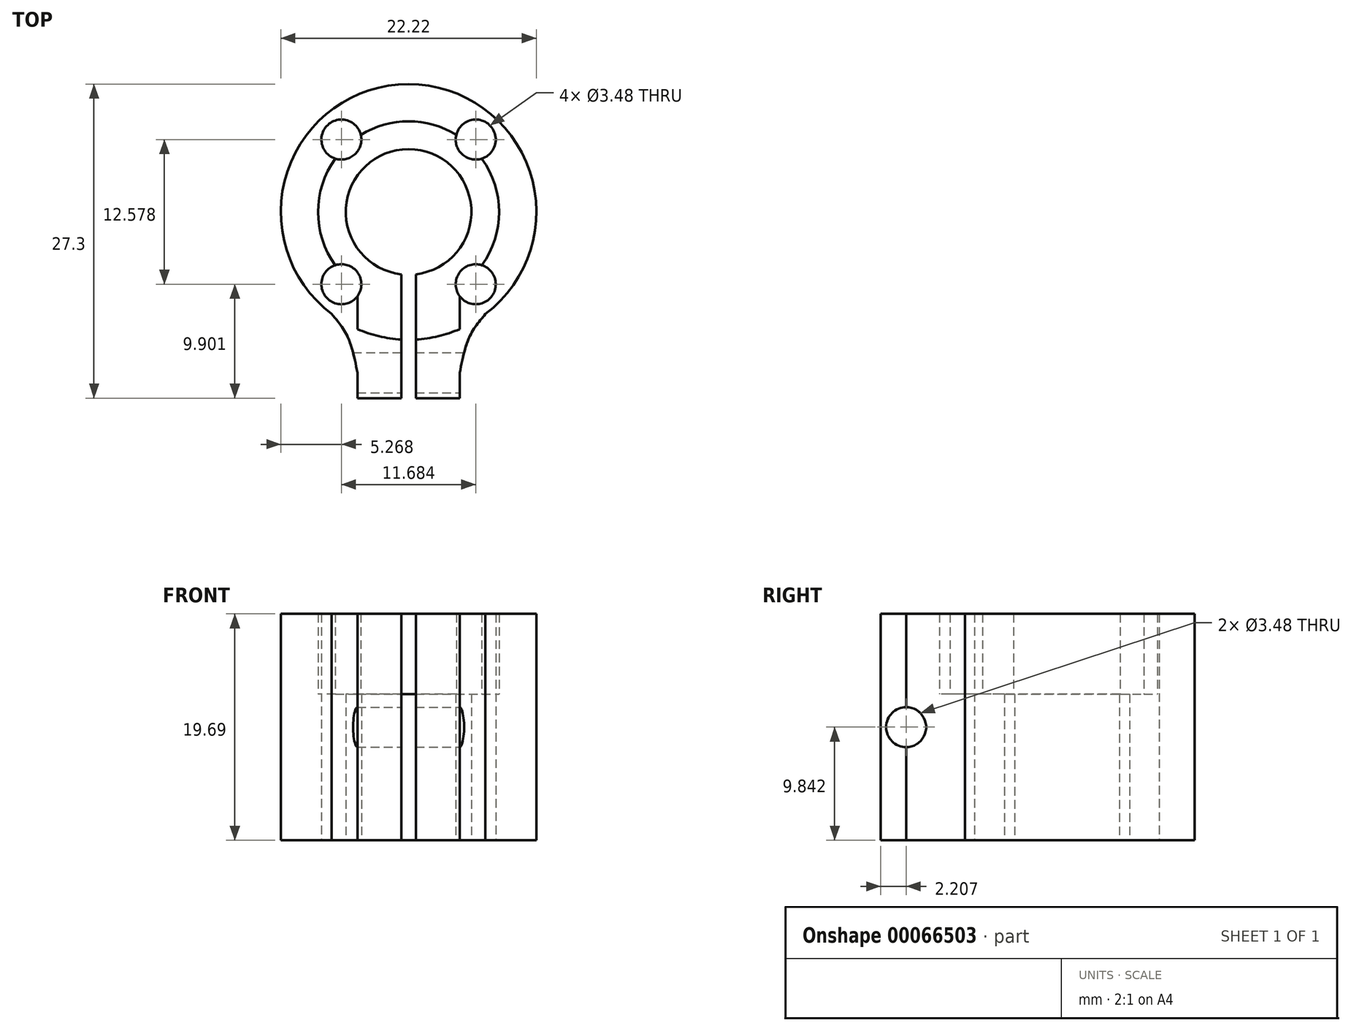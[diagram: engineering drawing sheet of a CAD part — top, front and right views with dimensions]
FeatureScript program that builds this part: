
annotation { "Feature Type Name" : "Feature", "Feature Type Description" : "" }
export const myFeature = defineFeature(function(context is Context, id is Id, definition is map)
    precondition{}
    {
        {
            var Q0;
            Q0=qCreatedBy(makeId("Top.planeOp"),FACE);
            var sketch = newSketch(context, id + "F0", { "sketchPlane" : qUnion([Q0])});
            skCircle(sketch, "E0", {"center": v(0, 0) * mm, "radius": 11.11 * mm});
            skLineSegment(sketch, "E1.rect.bottom", {"start": v(4.45, -16.2) * mm, "end": v(-4.44, -16.2) * mm});
            skLineSegment(sketch, "E1.rect.top", {"start": v(4.44, 16.2) * mm, "end": v(-4.45, 16.2) * mm});
            skLineSegment(sketch, "E1.rect.left", {"start": v(4.44, -16.2) * mm, "end": v(4.44, 16.2) * mm});
            skLineSegment(sketch, "E1.rect.right", {"start": v(-4.45, -16.2) * mm, "end": v(-4.44, 16.2) * mm});
            skLineSegment(sketch, "E2.rect.bottom", {"start": v(-0.63, 16.2) * mm, "end": v(0.63, 16.2) * mm});
            skLineSegment(sketch, "E2.rect.top", {"start": v(-0.63, -16.2) * mm, "end": v(0.63, -16.2) * mm});
            skLineSegment(sketch, "E2.rect.left", {"start": v(-0.63, 16.2) * mm, "end": v(-0.63, -16.2) * mm});
            skLineSegment(sketch, "E2.rect.right", {"start": v(0.63, 16.2) * mm, "end": v(0.63, -16.2) * mm});
            skLineSegment(sketch, "E3", {"start": v(0, 24.4) * mm, "end": v(0, -38.1) * mm, "construction": true});
            skFitSpline(sketch, "E4", {"points": [v(-6.69, -8.88) * mm, v(-5.33, -10.8) * mm, v(-4.45, -13.98) * mm], "startDerivative": vector(3.26, -3.85) * mm, "endDerivative": vector(1.27, -6.31) * mm});
            skFitSpline(sketch, "E5.MirrorCS", {"points": [v(6.69, -8.88) * mm, v(5.33, -10.8) * mm, v(4.45, -13.98) * mm], "startDerivative": vector(-3.26, -3.85) * mm, "endDerivative": vector(-1.27, -6.31) * mm});
            skCircle(sketch, "E6", {"center": v(-5.84, 6.29) * mm, "radius": 1.74 * mm});
            skCircle(sketch, "E7.MirrorC", {"center": v(5.84, 6.29) * mm, "radius": 1.74 * mm});
            skCircle(sketch, "E8.MirrorC", {"center": v(-5.84, -6.29) * mm, "radius": 1.74 * mm});
            skCircle(sketch, "E9.MirrorC", {"center": v(5.84, -6.29) * mm, "radius": 1.74 * mm});
            skCircle(sketch, "E10", {"center": v(0, 0) * mm, "radius": 7.87 * mm});
            skCircle(sketch, "E11", {"center": v(0, 0) * mm, "radius": 5.46 * mm});
            skSolve(sketch);
        }
        {
            var Q0;
            {var subQ0=sQuery(id+"F0.wireOp",EDGE,"E0");var subQ1=makeQuery(id+"F0.imprint","INTERSECT",VERTEX,{"derivedFrom":[subQ0,sQuery(id+"F0.wireOp",EDGE,"E4")]});Q0=makeQuery(id+"F0.imprint","IMPRINT",FACE,{"disambiguationData":[TD([[makeQuery(id+"F0.imprint","IMPRINT",EDGE,{"disambiguationData":[TD([[subQ1,1.0]])],"derivedFrom":subQ0}),1.0]])]});}
            var Q1;
            {var subQ1=sQuery(id+"F0.wireOp",EDGE,"E0");var subQ5=sQuery(id+"F0.wireOp",EDGE,"E1.rect.right");var subQ6=makeQuery(id+"F0.imprint","INTERSECT",VERTEX,{"disambiguationData":[OD(0.0)],"derivedFrom":[subQ1,subQ5]});Q1=makeQuery(id+"F0.imprint","IMPRINT",FACE,{"disambiguationData":[TD([[makeQuery(id+"F0.imprint","IMPRINT",EDGE,{"disambiguationData":[TD([[subQ6,1.0]])],"derivedFrom":subQ1}),1.0]])]});}
            var Q2;
            {var subQ1=sQuery(id+"F0.wireOp",EDGE,"E0");var subQ6=sQuery(id+"F0.wireOp",EDGE,"E1.rect.left");var subQ8=makeQuery(id+"F0.imprint","INTERSECT",VERTEX,{"disambiguationData":[OD(0.0)],"derivedFrom":[subQ1,subQ6]});Q2=makeQuery(id+"F0.imprint","IMPRINT",FACE,{"disambiguationData":[TD([[makeQuery(id+"F0.imprint","IMPRINT",EDGE,{"disambiguationData":[TD([[subQ8,-1.0]])],"derivedFrom":subQ1}),1.0]])]});}
            var Q3;
            {var subQ0=sQuery(id+"F0.wireOp",EDGE,"E0");var subQ1=makeQuery(id+"F0.imprint","INTERSECT",VERTEX,{"derivedFrom":[subQ0,sQuery(id+"F0.wireOp",EDGE,"E5.MirrorCS")]});Q3=makeQuery(id+"F0.imprint","IMPRINT",FACE,{"disambiguationData":[TD([[makeQuery(id+"F0.imprint","IMPRINT",EDGE,{"disambiguationData":[TD([[subQ1,1.0]])],"derivedFrom":subQ0}),1.0]])]});}
            var Q4;
            {var subQ0=sQuery(id+"F0.wireOp",EDGE,"E2.rect.right");var subQ1=sQuery(id+"F0.wireOp",EDGE,"E0");var subQ2=makeQuery(id+"F0.imprint","INTERSECT",VERTEX,{"disambiguationData":[OD(0.0)],"derivedFrom":[subQ1,subQ0]});Q4=makeQuery(id+"F0.imprint","IMPRINT",FACE,{"disambiguationData":[TD([[makeQuery(id+"F0.imprint","IMPRINT",EDGE,{"disambiguationData":[TD([[subQ2,-1.0]])],"derivedFrom":subQ1}),1.0]])]});}
            var Q5;
            {var subQ0=sQuery(id+"F0.wireOp",EDGE,"E4");Q5=makeQuery(id+"F0.imprint","IMPRINT",FACE,{"disambiguationData":[TD([[makeQuery(id+"F0.imprint","IMPRINT",EDGE,{"derivedFrom":subQ0}),1.0]])]});}
            var Q6;
            {var subQ0=sQuery(id+"F0.wireOp",EDGE,"E1.rect.right");var subQ6=sQuery(id+"F0.wireOp",EDGE,"E0");var subQ7=makeQuery(id+"F0.imprint","INTERSECT",VERTEX,{"disambiguationData":[OD(1.0)],"derivedFrom":[subQ6,subQ0]});Q6=makeQuery(id+"F0.imprint","IMPRINT",FACE,{"disambiguationData":[TD([[makeQuery(id+"F0.imprint","IMPRINT",EDGE,{"disambiguationData":[TD([[subQ7,-1.0]])],"derivedFrom":subQ6}),-1.0]])]});}
            var Q7;
            {var subQ2=sQuery(id+"F0.wireOp",EDGE,"E0");var subQ6=sQuery(id+"F0.wireOp",EDGE,"E2.rect.right");var subQ7=makeQuery(id+"F0.imprint","INTERSECT",VERTEX,{"disambiguationData":[OD(1.0)],"derivedFrom":[subQ2,subQ6]});Q7=makeQuery(id+"F0.imprint","IMPRINT",FACE,{"disambiguationData":[TD([[makeQuery(id+"F0.imprint","IMPRINT",EDGE,{"disambiguationData":[TD([[subQ7,-1.0]])],"derivedFrom":subQ2}),-1.0]])]});}
            var Q8;
            {var subQ0=sQuery(id+"F0.wireOp",EDGE,"E5.MirrorCS");Q8=makeQuery(id+"F0.imprint","IMPRINT",FACE,{"disambiguationData":[TD([[makeQuery(id+"F0.imprint","IMPRINT",EDGE,{"derivedFrom":subQ0}),-1.0]])]});}
            extrude(context, id + "F1", {"entities" : qUnion([Q0, Q1, Q2, Q3, Q4, Q5, Q6, Q7, Q8]), "depth" : 7 * mm});
        }
        {
            var Q0;
            {var subQ0=sQuery(id+"F0.wireOp",EDGE,"E8.MirrorC");var subQ1=sQuery(id+"F0.wireOp",EDGE,"E1.rect.right");var subQ2=makeQuery(id+"F0.imprint","INTERSECT",VERTEX,{"disambiguationData":[OD(1.0)],"derivedFrom":[subQ1,subQ0]});Q0=makeQuery(id+"F0.imprint","IMPRINT",FACE,{"disambiguationData":[TD([[makeQuery(id+"F0.imprint","IMPRINT",EDGE,{"disambiguationData":[TD([[subQ2,-1.0]])],"derivedFrom":subQ1}),1.0]])]});}
            var Q1;
            {var subQ5=sQuery(id+"F0.wireOp",EDGE,"E1.rect.right");var subQ7=sQuery(id+"F0.wireOp",EDGE,"E11");var subQ8=makeQuery(id+"F0.imprint","INTERSECT",VERTEX,{"disambiguationData":[OD(1.0)],"derivedFrom":[subQ5,subQ7]});Q1=makeQuery(id+"F0.imprint","IMPRINT",FACE,{"disambiguationData":[TD([[makeQuery(id+"F0.imprint","IMPRINT",EDGE,{"disambiguationData":[TD([[subQ8,-1.0]])],"derivedFrom":subQ5}),-1.0]])]});}
            var Q2;
            {var subQ5=sQuery(id+"F0.wireOp",EDGE,"E1.rect.left");var subQ7=sQuery(id+"F0.wireOp",EDGE,"E11");var subQ9=makeQuery(id+"F0.imprint","INTERSECT",VERTEX,{"disambiguationData":[OD(1.0)],"derivedFrom":[subQ5,subQ7]});Q2=makeQuery(id+"F0.imprint","IMPRINT",FACE,{"disambiguationData":[TD([[makeQuery(id+"F0.imprint","IMPRINT",EDGE,{"disambiguationData":[TD([[subQ9,-1.0]])],"derivedFrom":subQ5}),1.0]])]});}
            var Q3;
            {var subQ0=sQuery(id+"F0.wireOp",EDGE,"E9.MirrorC");var subQ1=sQuery(id+"F0.wireOp",EDGE,"E1.rect.left");var subQ2=makeQuery(id+"F0.imprint","INTERSECT",VERTEX,{"disambiguationData":[OD(1.0)],"derivedFrom":[subQ1,subQ0]});Q3=makeQuery(id+"F0.imprint","IMPRINT",FACE,{"disambiguationData":[TD([[makeQuery(id+"F0.imprint","IMPRINT",EDGE,{"disambiguationData":[TD([[subQ2,-1.0]])],"derivedFrom":subQ1}),-1.0]])]});}
            var Q4;
            {var subQ3=sQuery(id+"F0.wireOp",EDGE,"E9.MirrorC");var subQ5=sQuery(id+"F0.wireOp",EDGE,"E1.rect.left");var subQ6=makeQuery(id+"F0.imprint","INTERSECT",VERTEX,{"disambiguationData":[OD(1.0)],"derivedFrom":[subQ5,subQ3]});Q4=makeQuery(id+"F0.imprint","IMPRINT",FACE,{"disambiguationData":[TD([[makeQuery(id+"F0.imprint","IMPRINT",EDGE,{"disambiguationData":[TD([[subQ6,-1.0]])],"derivedFrom":subQ5}),1.0]])]});}
            var Q5;
            {var subQ3=sQuery(id+"F0.wireOp",EDGE,"E8.MirrorC");var subQ5=sQuery(id+"F0.wireOp",EDGE,"E1.rect.right");var subQ6=makeQuery(id+"F0.imprint","INTERSECT",VERTEX,{"disambiguationData":[OD(1.0)],"derivedFrom":[subQ5,subQ3]});Q5=makeQuery(id+"F0.imprint","IMPRINT",FACE,{"disambiguationData":[TD([[makeQuery(id+"F0.imprint","IMPRINT",EDGE,{"disambiguationData":[TD([[subQ6,-1.0]])],"derivedFrom":subQ5}),-1.0]])]});}
            var Q6;
            {var subQ1=sQuery(id+"F0.wireOp",EDGE,"E0");var subQ5=sQuery(id+"F0.wireOp",EDGE,"E1.rect.right");var subQ6=makeQuery(id+"F0.imprint","INTERSECT",VERTEX,{"disambiguationData":[OD(1.0)],"derivedFrom":[subQ1,subQ5]});Q6=makeQuery(id+"F0.imprint","IMPRINT",FACE,{"disambiguationData":[TD([[makeQuery(id+"F0.imprint","IMPRINT",EDGE,{"disambiguationData":[TD([[subQ6,-1.0]])],"derivedFrom":subQ1}),1.0]])]});}
            var Q7;
            {var subQ5=sQuery(id+"F0.wireOp",EDGE,"E0");var subQ7=sQuery(id+"F0.wireOp",EDGE,"E2.rect.right");var subQ8=makeQuery(id+"F0.imprint","INTERSECT",VERTEX,{"disambiguationData":[OD(1.0)],"derivedFrom":[subQ5,subQ7]});Q7=makeQuery(id+"F0.imprint","IMPRINT",FACE,{"disambiguationData":[TD([[makeQuery(id+"F0.imprint","IMPRINT",EDGE,{"disambiguationData":[TD([[subQ8,-1.0]])],"derivedFrom":subQ5}),1.0]])]});}
            var Q8;
            {var subQ1=sQuery(id+"F0.wireOp",EDGE,"E0");var subQ11=makeQuery(id+"F0.imprint","INTERSECT",VERTEX,{"derivedFrom":[subQ1,sQuery(id+"F0.wireOp",EDGE,"E5.MirrorCS")]});Q8=makeQuery(id+"F0.imprint","IMPRINT",FACE,{"disambiguationData":[TD([[makeQuery(id+"F0.imprint","IMPRINT",EDGE,{"disambiguationData":[TD([[subQ11,1.0]])],"derivedFrom":subQ1}),1.0]])]});}
            var Q9;
            {var subQ1=sQuery(id+"F0.wireOp",EDGE,"E1.rect.left");var subQ5=sQuery(id+"F0.wireOp",EDGE,"E0");var subQ6=makeQuery(id+"F0.imprint","INTERSECT",VERTEX,{"disambiguationData":[OD(0.0)],"derivedFrom":[subQ5,subQ1]});Q9=makeQuery(id+"F0.imprint","IMPRINT",FACE,{"disambiguationData":[TD([[makeQuery(id+"F0.imprint","IMPRINT",EDGE,{"disambiguationData":[TD([[subQ6,-1.0]])],"derivedFrom":subQ5}),1.0]])]});}
            var Q10;
            {var subQ1=sQuery(id+"F0.wireOp",EDGE,"E1.rect.right");var subQ6=sQuery(id+"F0.wireOp",EDGE,"E0");var subQ9=makeQuery(id+"F0.imprint","INTERSECT",VERTEX,{"disambiguationData":[OD(0.0)],"derivedFrom":[subQ6,subQ1]});Q10=makeQuery(id+"F0.imprint","IMPRINT",FACE,{"disambiguationData":[TD([[makeQuery(id+"F0.imprint","IMPRINT",EDGE,{"disambiguationData":[TD([[subQ9,1.0]])],"derivedFrom":subQ6}),1.0]])]});}
            var Q11;
            {var subQ1=sQuery(id+"F0.wireOp",EDGE,"E0");var subQ8=makeQuery(id+"F0.imprint","INTERSECT",VERTEX,{"derivedFrom":[subQ1,sQuery(id+"F0.wireOp",EDGE,"E4")]});Q11=makeQuery(id+"F0.imprint","IMPRINT",FACE,{"disambiguationData":[TD([[makeQuery(id+"F0.imprint","IMPRINT",EDGE,{"disambiguationData":[TD([[subQ8,1.0]])],"derivedFrom":subQ1}),1.0]])]});}
            var Q12;
            {var subQ0=sQuery(id+"F0.wireOp",EDGE,"E2.rect.right");var subQ1=sQuery(id+"F0.wireOp",EDGE,"E0");var subQ2=makeQuery(id+"F0.imprint","INTERSECT",VERTEX,{"disambiguationData":[OD(0.0)],"derivedFrom":[subQ1,subQ0]});Q12=makeQuery(id+"F0.imprint","IMPRINT",FACE,{"disambiguationData":[TD([[makeQuery(id+"F0.imprint","IMPRINT",EDGE,{"disambiguationData":[TD([[subQ2,-1.0]])],"derivedFrom":subQ1}),1.0]])]});}
            var Q13;
            {var subQ0=sQuery(id+"F0.wireOp",EDGE,"E10");var subQ1=sQuery(id+"F0.wireOp",EDGE,"E2.rect.left");var subQ2=makeQuery(id+"F0.imprint","INTERSECT",VERTEX,{"disambiguationData":[OD(0.0)],"derivedFrom":[subQ1,subQ0]});Q13=makeQuery(id+"F0.imprint","IMPRINT",FACE,{"disambiguationData":[TD([[makeQuery(id+"F0.imprint","IMPRINT",EDGE,{"disambiguationData":[TD([[subQ2,-1.0]])],"derivedFrom":subQ1}),1.0]])]});}
            var Q14;
            Q14=makeQuery(id+"F1.opExtrude","CAP_FACE",FACE,{"disambiguationData":[OSD([sQuery(id+"F0.wireOp",EDGE,"E0"),sQuery(id+"F0.wireOp",EDGE,"E1.rect.bottom"),sQuery(id+"F0.wireOp",EDGE,"E1.rect.left"),sQuery(id+"F0.wireOp",EDGE,"E1.rect.right"),sQuery(id+"F0.wireOp",EDGE,"E2.rect.left"),sQuery(id+"F0.wireOp",EDGE,"E2.rect.right"),sQuery(id+"F0.wireOp",EDGE,"E4"),sQuery(id+"F0.wireOp",EDGE,"E5.MirrorCS"),sQuery(id+"F0.wireOp",EDGE,"E6"),sQuery(id+"F0.wireOp",EDGE,"E7.MirrorC"),sQuery(id+"F0.wireOp",EDGE,"E8.MirrorC"),sQuery(id+"F0.wireOp",EDGE,"E9.MirrorC"),sQuery(id+"F0.wireOp",EDGE,"E10")])],"isStart":false});
            extrude(context, id + "F2", {"entities" : qUnion([Q0, Q1, Q2, Q3, Q4, Q5, Q6, Q7, Q8, Q9, Q10, Q11, Q12, Q13, Q14]), "operationType" : NewBodyOperationType.ADD, "depth" : 12.7 * mm});
        }
        {
            var Q0;
            {var subQ0=sQuery(id+"F0.wireOp",EDGE,"E1.rect.left");var subQ1=makeQuery(id+"F0.imprint","IMPRINT",EDGE,{"disambiguationData":[TD([[makeQuery(id+"F0.imprint","INTERSECT",VERTEX,{"derivedFrom":[sQuery(id+"F0.wireOp",EDGE,"E1.rect.bottom"),subQ0]}),-1.0]])],"derivedFrom":subQ0});Q0=makeQuery(id+"F2.boolean.opBoolean","MERGE",FACE,{"derivedFrom":[makeQuery(id+"F1.opExtrude","SWEPT_FACE",FACE,{"disambiguationData":[OSD([subQ0]),TDD([subQ1])]}),makeQuery(id+"F2.opExtrude","SWEPT_FACE",FACE,{"disambiguationData":[OSD([subQ0]),TDD([makeQuery(id+"F1.opExtrude","CAP_EDGE",EDGE,{"disambiguationData":[OSD([subQ0]),TDD([subQ1])],"isStart":false})])]})]});}
            var sketch = newSketch(context, id + "F3", { "sketchPlane" : qUnion([Q0])});
            skCircle(sketch, "E12", {"center": v(-13.98, 9.84) * mm, "radius": 1.74 * mm});
            skSolve(sketch);
        }
        {
            var Q0;
            Q0 = qSketchRegion(id + "F3", true);
            extrude(context, id + "F4", {"entities" : qUnion([Q0]), "operationType" : NewBodyOperationType.REMOVE, "oppositeDirection" : true, "depth" : 25.4 * mm, "hasSecondDirection" : true, "secondDirectionOppositeDirection" : false, "secondDirectionDepth" : 25.4 * mm});
        }
    });
